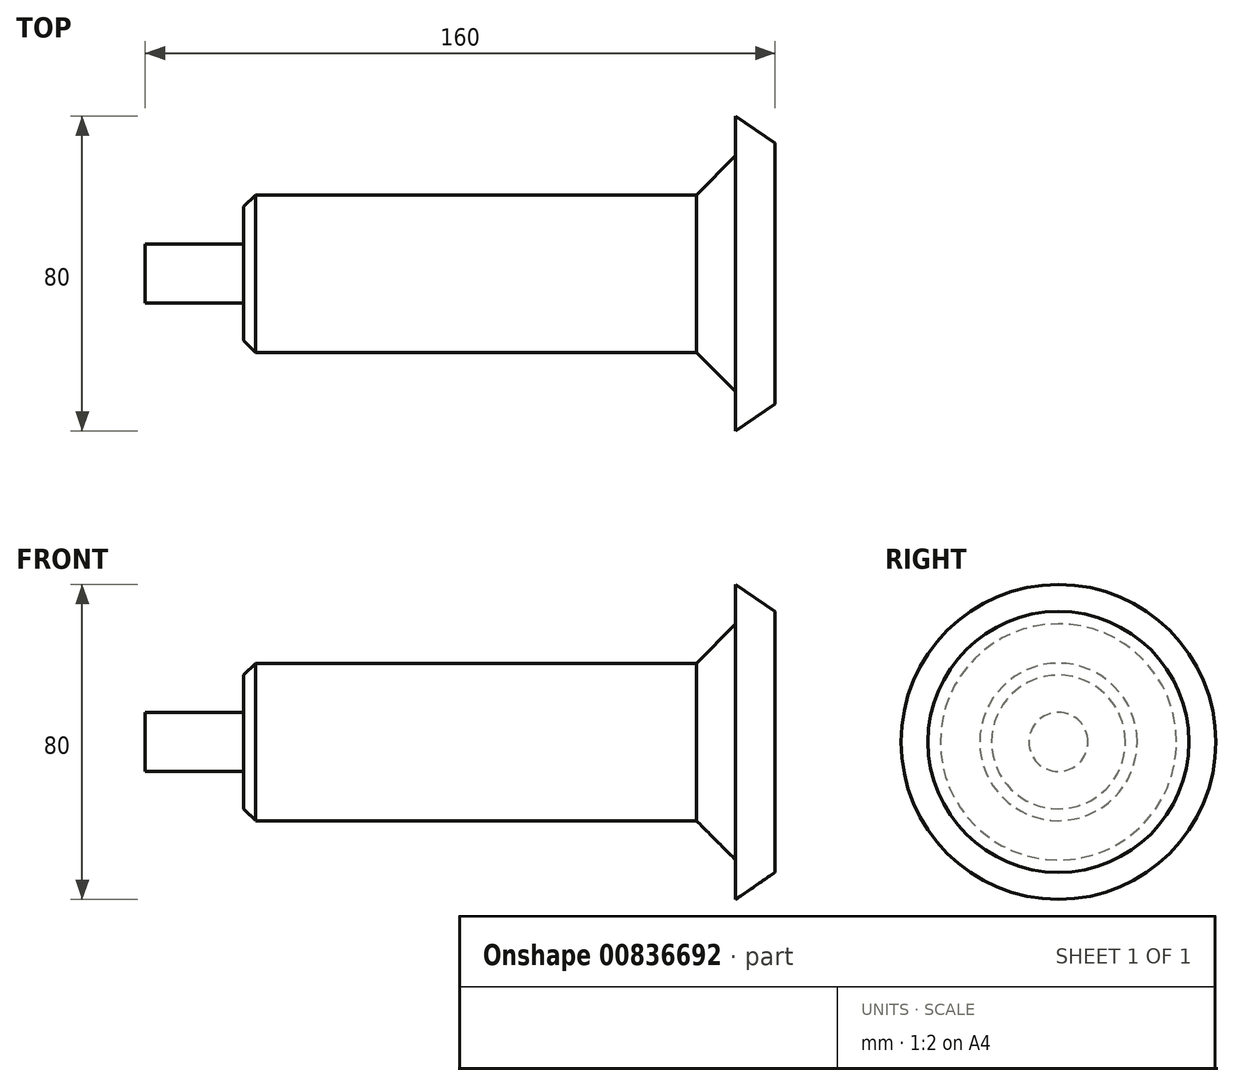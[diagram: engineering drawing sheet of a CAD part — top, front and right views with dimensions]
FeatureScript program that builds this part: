
annotation { "Feature Type Name" : "Feature", "Feature Type Description" : "" }
export const myFeature = defineFeature(function(context is Context, id is Id, definition is map)
    precondition{}
    {
        {
            var Q0;
            Q0=qCreatedBy(makeId("Top.planeOp"),FACE);
            var sketch = newSketch(context, id + "F0", { "sketchPlane" : qUnion([Q0])});
            skLineSegment(sketch, "E0", {"start": v(0, 0) * mm, "end": v(0, 7.5) * mm});
            skLineSegment(sketch, "E1", {"start": v(0, 7.5) * mm, "end": v(25, 7.5) * mm});
            skLineSegment(sketch, "E2", {"start": v(25, 7.5) * mm, "end": v(25, 17) * mm});
            skLineSegment(sketch, "E3", {"start": v(25, 17) * mm, "end": v(28, 20) * mm});
            skLineSegment(sketch, "E4", {"start": v(28, 20) * mm, "end": v(140, 20) * mm});
            skLineSegment(sketch, "E5", {"start": v(140, 20) * mm, "end": v(150, 30) * mm});
            skLineSegment(sketch, "E6", {"start": v(150, 30) * mm, "end": v(150, 40) * mm});
            skLineSegment(sketch, "E7", {"start": v(150, 40) * mm, "end": v(160, 33.14) * mm});
            skLineSegment(sketch, "E8", {"start": v(160, 33.14) * mm, "end": v(160, 0) * mm});
            skLineSegment(sketch, "E9", {"start": v(160, 0) * mm, "end": v(0, 0) * mm});
            skSolve(sketch);
        }
        {
            var Q0;
            Q0=makeQuery(id+"F0.imprint","IMPRINT",FACE,{"disambiguationData":[TD([[makeQuery(id+"F0.imprint","IMPRINT",EDGE,{"derivedFrom":sQuery(id+"F0.wireOp",EDGE,"E0")}),-1.0]])]});
            var Q1;
            Q1=sQuery(id+"F0.wireOp",EDGE,"E9");
            revolve(context, id + "F1", {"surfaceOperationType" : NewSurfaceOperationType.NEW, "entities" : qUnion([Q0]), "axis" : qUnion([Q1]), "revolveType" : RevolveType.FULL});
        }
    });
